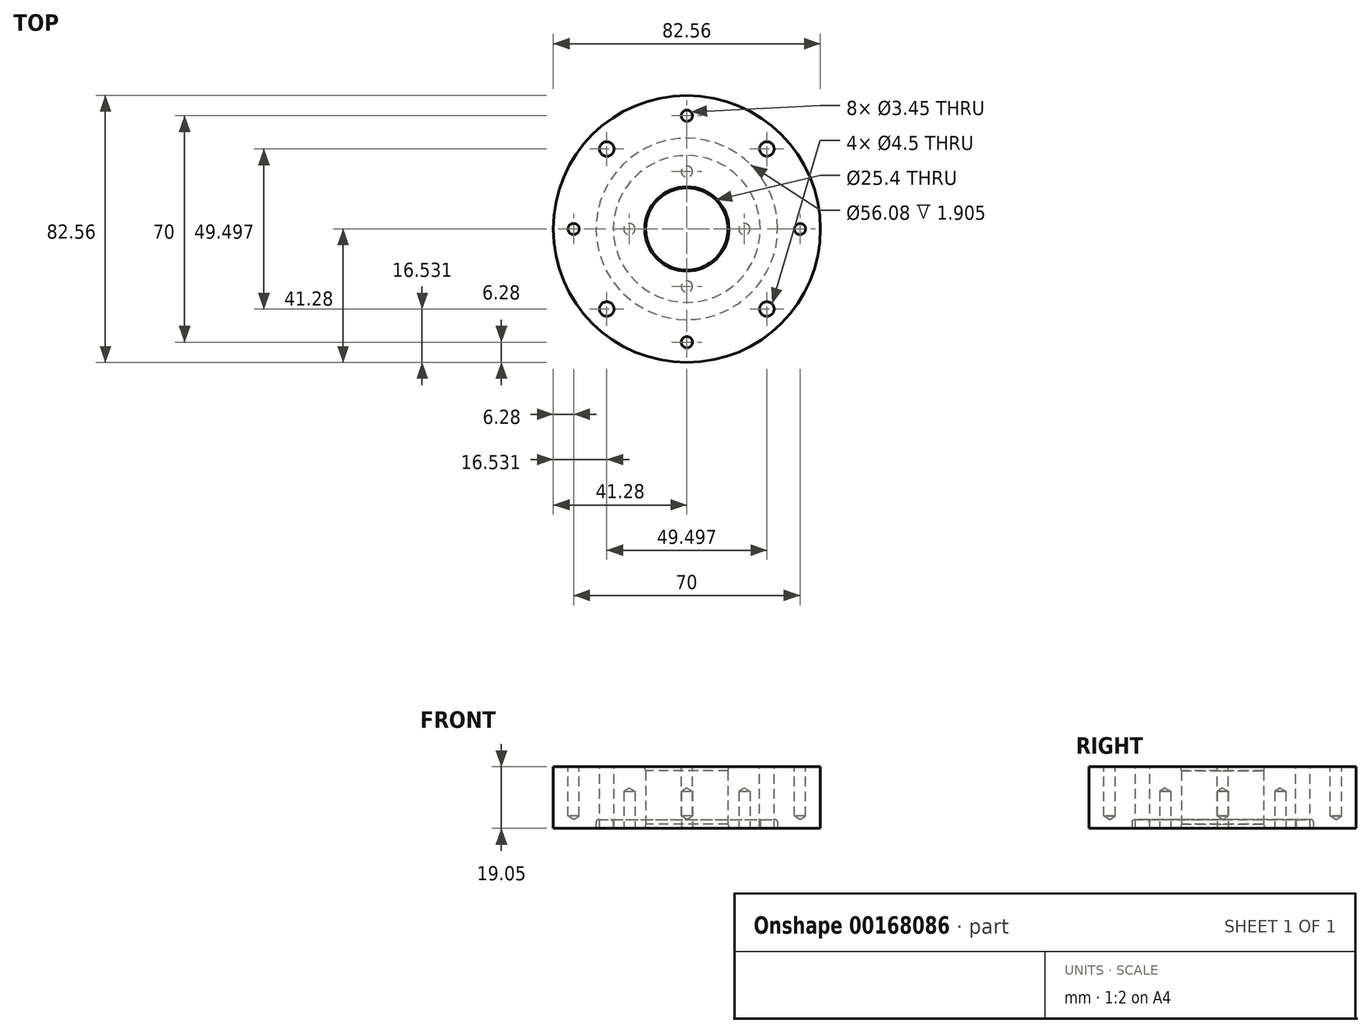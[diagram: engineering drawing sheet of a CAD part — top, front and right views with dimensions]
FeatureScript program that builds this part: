
annotation { "Feature Type Name" : "Feature", "Feature Type Description" : "" }
export const myFeature = defineFeature(function(context is Context, id is Id, definition is map)
    precondition{}
    {
        {
            var Q0;
            Q0=qCreatedBy(makeId("Top.planeOp"),FACE);
            var sketch = newSketch(context, id + "F0", { "sketchPlane" : qUnion([Q0])});
            skCircle(sketch, "E0", {"center": v(0, 0) * mm, "radius": 41.28 * mm});
            skCircle(sketch, "E1", {"center": v(0, 0) * mm, "radius": 12.7 * mm});
            skSolve(sketch);
        }
        {
            var Q0;
            Q0=qSketchRegion(id+"F0",true);
            extrude(context, id + "F1", {"entities" : qUnion([Q0]), "depth" : 19.05 * mm});
        }
        {
            var Q0;
            Q0=makeQuery(id+"F1.opExtrude","CAP_EDGE",EDGE,{"disambiguationData":[OSD([sQuery(id+"F0.wireOp",EDGE,"E1")])],"isStart":false});
            var Q1;
            Q1=makeQuery(id+"F1.opExtrude","CAP_EDGE",EDGE,{"disambiguationData":[OSD([sQuery(id+"F0.wireOp",EDGE,"E1")])],"isStart":true});
            chamfer(context, id + "F2", {"entities" : qUnion([Q0, Q1]), "chamferType" : ChamferType.OFFSET_ANGLE, "width" : 1.27 * mm, "oppositeDirection" : false, "angle" : 15 * degree, "tangentPropagation" : true});
        }
        {
            var Q0;
            Q0=makeQuery(id+"F1.opExtrude","CAP_FACE",FACE,{"disambiguationData":[OSD([sQuery(id+"F0.wireOp",EDGE,"E0"),sQuery(id+"F0.wireOp",EDGE,"E1")])],"isStart":true});
            var sketch = newSketch(context, id + "F3", { "sketchPlane" : qUnion([Q0])});
            skLineSegment(sketch, "E2", {"start": v(0, 0) * mm, "end": v(0, -12.7) * mm, "construction": true});
            skLineSegment(sketch, "E3", {"start": v(0, -12.7) * mm, "end": v(0, -22.86) * mm, "construction": true});
            skLineSegment(sketch, "E4", {"start": v(0, -22.86) * mm, "end": v(0, -12.7) * mm, "construction": true});
            skPoint(sketch, "E5", {"position": v(0, -17.78) * mm});
            skPoint(sketch, "E6.1.0", {"position": v(17.78, 0) * mm});
            skPoint(sketch, "E6.2.0", {"position": v(0, 17.78) * mm});
            skPoint(sketch, "E6.3.0", {"position": v(-17.78, 0) * mm});
            skPoint(sketch, "E6.center", {"position": v(0, 0) * mm});
            skSolve(sketch);
        }
        {
            var Q0;
            Q0=sQuery(id+"F3.wireOp",VERTEX,"E5");
            var Q1;
            Q1=sQuery(id+"F3.wireOp",VERTEX,"E6.3.0");
            var Q2;
            Q2=sQuery(id+"F3.wireOp",VERTEX,"E6.2.0");
            var Q3;
            Q3=sQuery(id+"F3.wireOp",VERTEX,"E6.1.0");
            var Q4;
            Q4=makeQuery(id+"F1.opExtrude","SWEPT_BODY",BODY,{"disambiguationData":[OSD([sQuery(id+"F0.wireOp",EDGE,"E0"),sQuery(id+"F0.wireOp",EDGE,"E1")])]});
            hole(context, id + "F4", {"style" : HoleStyle.SIMPLE, "endStyle" : HoleEndStyle.BLIND, "standardTappedOrClearance" : lookupTablePath({ "standard" : "ANSI", "engagement" : "75%", "pitch" : "32 tpi", "size" : "#8", "type" : "Tapped" }), "standardBlindInLast" : lookupTablePath({ "standard" : "ANSI", "engagement" : "75%", "pitch" : "32 tpi", "size" : "#8", "type" : "Tapped" }), "holeDiameter" : 3.45 * mm, "holeDepth" : 11.43 * mm, "locations" : qUnion([Q0, Q1, Q2, Q3]), "scope" : qUnion([Q4]), "majorDiameter" : 4.17 * mm});
        }
        {
            var Q0;
            Q0=makeQuery(id+"F1.opExtrude","CAP_FACE",FACE,{"disambiguationData":[OSD([sQuery(id+"F0.wireOp",EDGE,"E0"),sQuery(id+"F0.wireOp",EDGE,"E1")])],"isStart":false});
            var sketch = newSketch(context, id + "F5", { "sketchPlane" : qUnion([Q0])});
            skLineSegment(sketch, "E7", {"start": v(0, 0) * mm, "end": v(35, 0) * mm});
            skPoint(sketch, "E8", {"position": v(35, 0) * mm});
            skPoint(sketch, "E9.1.0", {"position": v(0, 35) * mm});
            skPoint(sketch, "E9.2.0", {"position": v(-35, 0) * mm});
            skPoint(sketch, "E9.3.0", {"position": v(0, -35) * mm});
            skPoint(sketch, "E9.center", {"position": v(0, 0) * mm});
            skSolve(sketch);
        }
        {
            var Q0;
            Q0=sQuery(id+"F5.wireOp",VERTEX,"E8");
            var Q1;
            Q1=sQuery(id+"F5.wireOp",VERTEX,"E9.3.0");
            var Q2;
            Q2=sQuery(id+"F5.wireOp",VERTEX,"E9.2.0");
            var Q3;
            Q3=sQuery(id+"F5.wireOp",VERTEX,"E9.1.0");
            var Q4;
            Q4=makeQuery(id+"F1.opExtrude","SWEPT_BODY",BODY,{"disambiguationData":[OSD([sQuery(id+"F0.wireOp",EDGE,"E0"),sQuery(id+"F0.wireOp",EDGE,"E1")])]});
            hole(context, id + "F6", {"style" : HoleStyle.SIMPLE, "endStyle" : HoleEndStyle.BLIND, "standardTappedOrClearance" : lookupTablePath({ "standard" : "ANSI", "engagement" : "75%", "pitch" : "32 tpi", "size" : "#8", "type" : "Tapped" }), "standardBlindInLast" : lookupTablePath({ "standard" : "ANSI", "engagement" : "75%", "pitch" : "32 tpi", "size" : "#8", "type" : "Tapped" }), "holeDiameter" : 3.45 * mm, "holeDepth" : 15.24 * mm, "locations" : qUnion([Q0, Q1, Q2, Q3]), "scope" : qUnion([Q4]), "majorDiameter" : 4.17 * mm});
        }
        {
            var Q0;
            Q0=makeQuery(id+"F1.opExtrude","CAP_FACE",FACE,{"disambiguationData":[OSD([sQuery(id+"F0.wireOp",EDGE,"E0"),sQuery(id+"F0.wireOp",EDGE,"E1")])],"isStart":false});
            var sketch = newSketch(context, id + "F7", { "sketchPlane" : qUnion([Q0])});
            skLineSegment(sketch, "E10", {"start": v(0, 0) * mm, "end": v(24.75, -24.75) * mm, "construction": true});
            skPoint(sketch, "E11", {"position": v(24.75, -24.75) * mm});
            skPoint(sketch, "E12.1.0", {"position": v(24.75, 24.75) * mm});
            skPoint(sketch, "E12.2.0", {"position": v(-24.75, 24.75) * mm});
            skPoint(sketch, "E12.3.0", {"position": v(-24.75, -24.75) * mm});
            skPoint(sketch, "E12.center", {"position": v(0, 0) * mm});
            skSolve(sketch);
        }
        {
            var Q0;
            Q0=sQuery(id+"F7.wireOp",VERTEX,"E11");
            var Q1;
            Q1=sQuery(id+"F7.wireOp",VERTEX,"E12.3.0");
            var Q2;
            Q2=sQuery(id+"F7.wireOp",VERTEX,"E12.2.0");
            var Q3;
            Q3=sQuery(id+"F7.wireOp",VERTEX,"E12.1.0");
            var Q4;
            Q4=makeQuery(id+"F1.opExtrude","SWEPT_BODY",BODY,{"disambiguationData":[OSD([sQuery(id+"F0.wireOp",EDGE,"E0"),sQuery(id+"F0.wireOp",EDGE,"E1")])]});
            hole(context, id + "F8", {"style" : HoleStyle.SIMPLE, "endStyle" : HoleEndStyle.THROUGH, "standardTappedOrClearance" : lookupTablePath({ "standard" : "ANSI", "fit" : "Normal (ASME)", "size" : "#8", "type" : "Clearance" }), "standardBlindInLast" : lookupTablePath({ "fit" : "Free", "standard" : "ANSI", "size" : "#8", "type" : "Clearance" }), "holeDiameter" : 4.5 * mm, "locations" : qUnion([Q0, Q1, Q2, Q3]), "scope" : qUnion([Q4]), "isTappedThrough" : true});
        }
        {
            var Q0;
            Q0=makeQuery(id+"F1.opExtrude","CAP_FACE",FACE,{"disambiguationData":[OSD([sQuery(id+"F0.wireOp",EDGE,"E0"),sQuery(id+"F0.wireOp",EDGE,"E1")])],"isStart":true});
            var sketch = newSketch(context, id + "F9", { "sketchPlane" : qUnion([Q0])});
            skCircle(sketch, "E13", {"center": v(0, 0) * mm, "radius": 22.7 * mm});
            skCircle(sketch, "E14", {"center": v(0, 0) * mm, "radius": 28.04 * mm});
            skCircle(sketch, "E15", {"center": v(0, 0) * mm, "radius": 25.37 * mm, "construction": true});
            skSolve(sketch);
        }
        {
            var Q0;
            Q0=qSketchRegion(id+"F9",true);
            extrude(context, id + "F10", {"entities" : qUnion([Q0]), "operationType" : NewBodyOperationType.REMOVE, "oppositeDirection" : true, "depth" : 2.7 * mm});
        }
        {
            var Q0;
            Q0=makeQuery(id+"F10.boolean.opBoolean","COPY",EDGE,{"derivedFrom":makeQuery(id+"F10.opExtrude","CAP_EDGE",EDGE,{"disambiguationData":[OSD([sQuery(id+"F9.wireOp",EDGE,"E13")])],"isStart":false})});
            var Q1;
            Q1=makeQuery(id+"F10.boolean.opBoolean","COPY",EDGE,{"derivedFrom":makeQuery(id+"F10.opExtrude","CAP_EDGE",EDGE,{"disambiguationData":[OSD([sQuery(id+"F9.wireOp",EDGE,"E14")])],"isStart":false})});
            fillet(context, id + "F11", {"entities" : qUnion([Q0, Q1]), "radius" : 0.79 * mm, "tangentPropagation" : true, "allowEdgeOverflow" : false});
        }
    });
